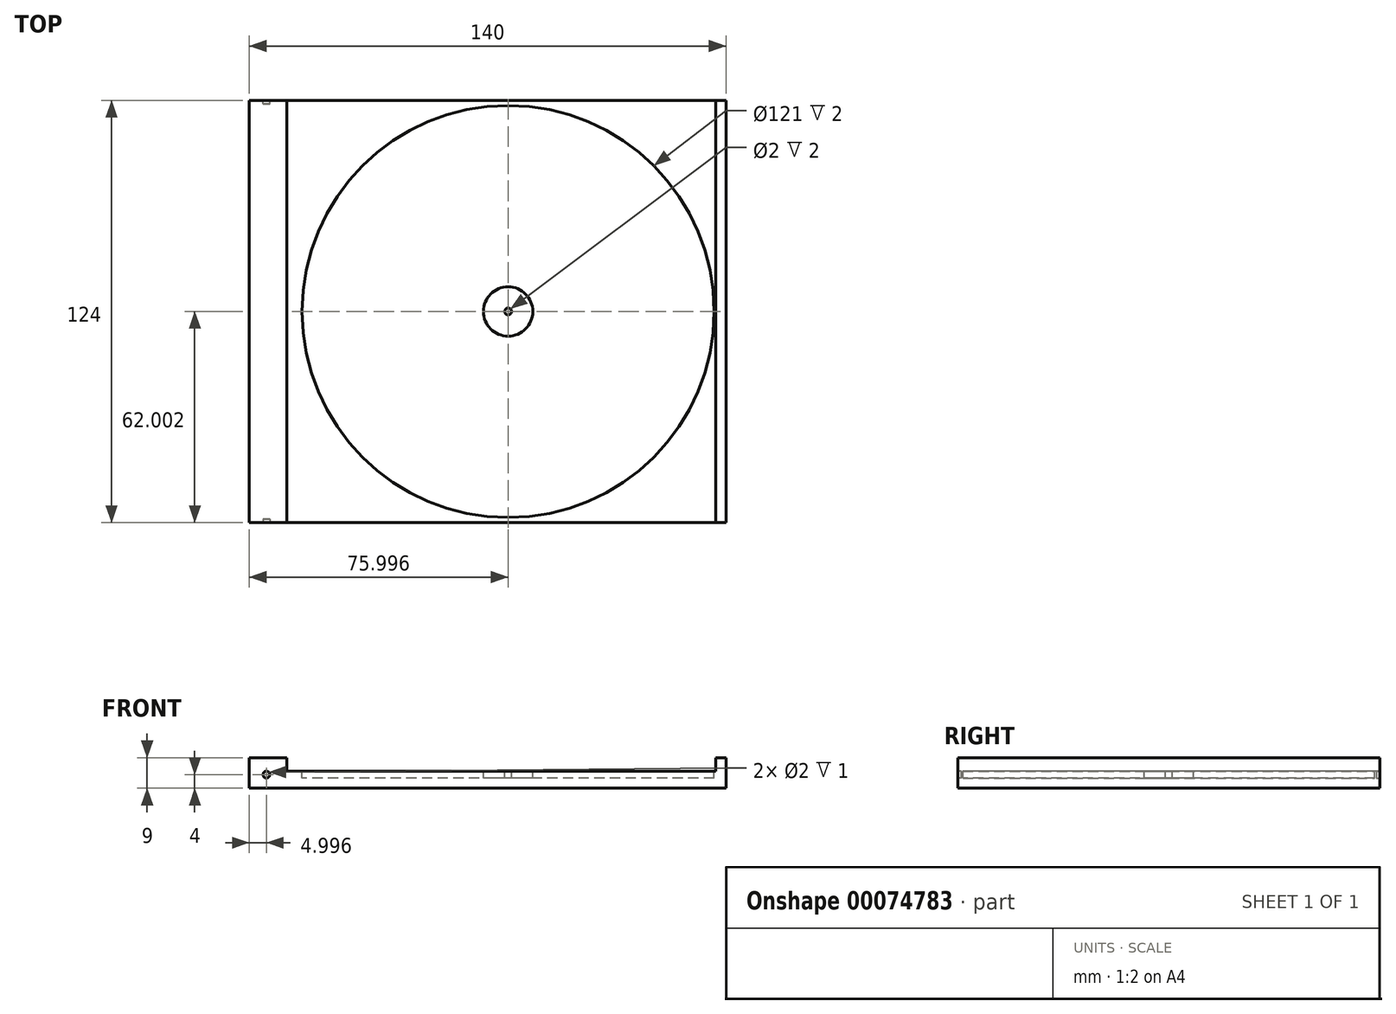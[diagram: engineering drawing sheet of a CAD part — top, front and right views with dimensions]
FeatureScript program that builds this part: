
annotation { "Feature Type Name" : "Feature", "Feature Type Description" : "" }
export const myFeature = defineFeature(function(context is Context, id is Id, definition is map)
    precondition{}
    {
        {
            var Q0;
            Q0=qCreatedBy(makeId("Top.planeOp"),FACE);
            var sketch = newSketch(context, id + "F0", { "sketchPlane" : qUnion([Q0])});
            skLineSegment(sketch, "E0.bottom", {"start": v(-67.85, 60.1) * mm, "end": v(72.15, 60.1) * mm});
            skLineSegment(sketch, "E0.top", {"start": v(-67.85, -63.9) * mm, "end": v(72.15, -63.9) * mm});
            skLineSegment(sketch, "E0.left", {"start": v(-67.85, 60.1) * mm, "end": v(-67.85, -63.9) * mm});
            skLineSegment(sketch, "E0.right", {"start": v(72.15, 60.1) * mm, "end": v(72.15, -63.9) * mm});
            skSolve(sketch);
        }
        {
            var Q0;
            Q0=makeQuery(id+"F0.imprint","IMPRINT",FACE,{"disambiguationData":[TD([[makeQuery(id+"F0.imprint","IMPRINT",EDGE,{"derivedFrom":sQuery(id+"F0.wireOp",EDGE,"E0.bottom")}),-1.0]])]});
            extrude(context, id + "F1", {"entities" : qUnion([Q0]), "depth" : 5 * mm});
        }
        {
            var Q0;
            Q0=makeQuery(id+"F1.opExtrude","CAP_FACE",FACE,{"disambiguationData":[OSD([sQuery(id+"F0.wireOp",EDGE,"E0.bottom"),sQuery(id+"F0.wireOp",EDGE,"E0.top"),sQuery(id+"F0.wireOp",EDGE,"E0.left"),sQuery(id+"F0.wireOp",EDGE,"E0.right")])],"isStart":false});
            var sketch = newSketch(context, id + "F2", { "sketchPlane" : qUnion([Q0])});
            skLineSegment(sketch, "E1.bottom", {"start": v(-67.85, 60.1) * mm, "end": v(-56.85, 60.1) * mm});
            skLineSegment(sketch, "E1.top", {"start": v(-67.85, -63.9) * mm, "end": v(-56.85, -63.9) * mm});
            skLineSegment(sketch, "E1.left", {"start": v(-67.85, 60.1) * mm, "end": v(-67.85, -63.9) * mm});
            skLineSegment(sketch, "E1.right", {"start": v(-56.85, 60.1) * mm, "end": v(-56.85, -63.9) * mm});
            skLineSegment(sketch, "E2.bottom", {"start": v(72.15, 60.1) * mm, "end": v(69.15, 60.1) * mm});
            skLineSegment(sketch, "E2.top", {"start": v(72.15, -63.9) * mm, "end": v(69.15, -63.9) * mm});
            skLineSegment(sketch, "E2.left", {"start": v(72.15, 60.1) * mm, "end": v(72.15, -63.9) * mm});
            skLineSegment(sketch, "E2.right", {"start": v(69.15, 60.1) * mm, "end": v(69.15, -63.9) * mm});
            skSolve(sketch);
        }
        {
            var Q0;
            Q0=makeQuery(id+"F2.imprint","IMPRINT",FACE,{"disambiguationData":[TD([[makeQuery(id+"F2.imprint","IMPRINT",EDGE,{"derivedFrom":sQuery(id+"F2.wireOp",EDGE,"E1.bottom")}),-1.0]])]});
            var Q1;
            Q1=makeQuery(id+"F2.imprint","IMPRINT",FACE,{"disambiguationData":[TD([[makeQuery(id+"F2.imprint","IMPRINT",EDGE,{"derivedFrom":sQuery(id+"F2.wireOp",EDGE,"E2.bottom")}),-1.0]])]});
            extrude(context, id + "F3", {"entities" : qUnion([Q0, Q1]), "operationType" : NewBodyOperationType.ADD, "depth" : 4 * mm});
        }
        {
            var Q0;
            Q0=makeQuery(id+"F1.opExtrude","CAP_FACE",FACE,{"disambiguationData":[OSD([sQuery(id+"F0.wireOp",EDGE,"E0.bottom"),sQuery(id+"F0.wireOp",EDGE,"E0.top"),sQuery(id+"F0.wireOp",EDGE,"E0.left"),sQuery(id+"F0.wireOp",EDGE,"E0.right")])],"isStart":false});
            var sketch = newSketch(context, id + "F4", { "sketchPlane" : qUnion([Q0])});
            skCircle(sketch, "E3", {"center": v(8.15, -1.9) * mm, "radius": 60.5 * mm});
            skCircle(sketch, "E4", {"center": v(8.15, -1.9) * mm, "radius": 7.25 * mm});
            skCircle(sketch, "E5", {"center": v(8.15, -1.9) * mm, "radius": 1 * mm});
            skSolve(sketch);
        }
        {
            var Q0;
            Q0=makeQuery(id+"F4.imprint","IMPRINT",FACE,{"disambiguationData":[TD([[makeQuery(id+"F4.imprint","IMPRINT",EDGE,{"derivedFrom":sQuery(id+"F4.wireOp",EDGE,"E3")}),1.0]])]});
            var Q1;
            Q1=makeQuery(id+"F4.imprint","IMPRINT",FACE,{"disambiguationData":[TD([[makeQuery(id+"F4.imprint","IMPRINT",EDGE,{"derivedFrom":sQuery(id+"F4.wireOp",EDGE,"E5")}),1.0]])]});
            extrude(context, id + "F5", {"entities" : qUnion([Q0, Q1]), "operationType" : NewBodyOperationType.REMOVE, "oppositeDirection" : true, "depth" : 2 * mm});
        }
        {
            var Q0;
            Q0=makeQuery(id+"F3.boolean.opBoolean","MERGE",FACE,{"derivedFrom":[makeQuery(id+"F1.opExtrude","SWEPT_FACE",FACE,{"disambiguationData":[OSD([sQuery(id+"F0.wireOp",EDGE,"E0.top")])]}),makeQuery(id+"F3.opExtrude","SWEPT_FACE",FACE,{"disambiguationData":[OSD([sQuery(id+"F2.wireOp",EDGE,"E1.top")])]}),makeQuery(id+"F3.opExtrude","SWEPT_FACE",FACE,{"disambiguationData":[OSD([sQuery(id+"F2.wireOp",EDGE,"E2.top")])]})]});
            var sketch = newSketch(context, id + "F6", { "sketchPlane" : qUnion([Q0])});
            skCircle(sketch, "E6", {"center": v(-62.85, 4) * mm, "radius": 1 * mm});
            skSolve(sketch);
        }
        {
            var Q0;
            Q0=makeQuery(id+"F6.imprint","IMPRINT",FACE,{"disambiguationData":[TD([[makeQuery(id+"F6.imprint","IMPRINT",EDGE,{"derivedFrom":sQuery(id+"F6.wireOp",EDGE,"E6")}),1.0]])]});
            extrude(context, id + "F7", {"entities" : qUnion([Q0]), "operationType" : NewBodyOperationType.REMOVE, "oppositeDirection" : true, "depth" : 1 * mm});
        }
        {
            var Q0;
            Q0=makeQuery(id+"F3.boolean.opBoolean","MERGE",FACE,{"derivedFrom":[makeQuery(id+"F1.opExtrude","SWEPT_FACE",FACE,{"disambiguationData":[OSD([sQuery(id+"F0.wireOp",EDGE,"E0.bottom")])]}),makeQuery(id+"F3.opExtrude","SWEPT_FACE",FACE,{"disambiguationData":[OSD([sQuery(id+"F2.wireOp",EDGE,"E1.bottom")])]}),makeQuery(id+"F3.opExtrude","SWEPT_FACE",FACE,{"disambiguationData":[OSD([sQuery(id+"F2.wireOp",EDGE,"E2.bottom")])]})]});
            var sketch = newSketch(context, id + "F8", { "sketchPlane" : qUnion([Q0])});
            skCircle(sketch, "E7", {"center": v(62.85, 4) * mm, "radius": 1 * mm});
            skSolve(sketch);
        }
        {
            var Q0;
            Q0=makeQuery(id+"F8.imprint","IMPRINT",FACE,{"disambiguationData":[TD([[makeQuery(id+"F8.imprint","IMPRINT",EDGE,{"derivedFrom":sQuery(id+"F8.wireOp",EDGE,"E7")}),1.0]])]});
            extrude(context, id + "F9", {"entities" : qUnion([Q0]), "operationType" : NewBodyOperationType.REMOVE, "oppositeDirection" : true, "depth" : 1 * mm});
        }
    });
